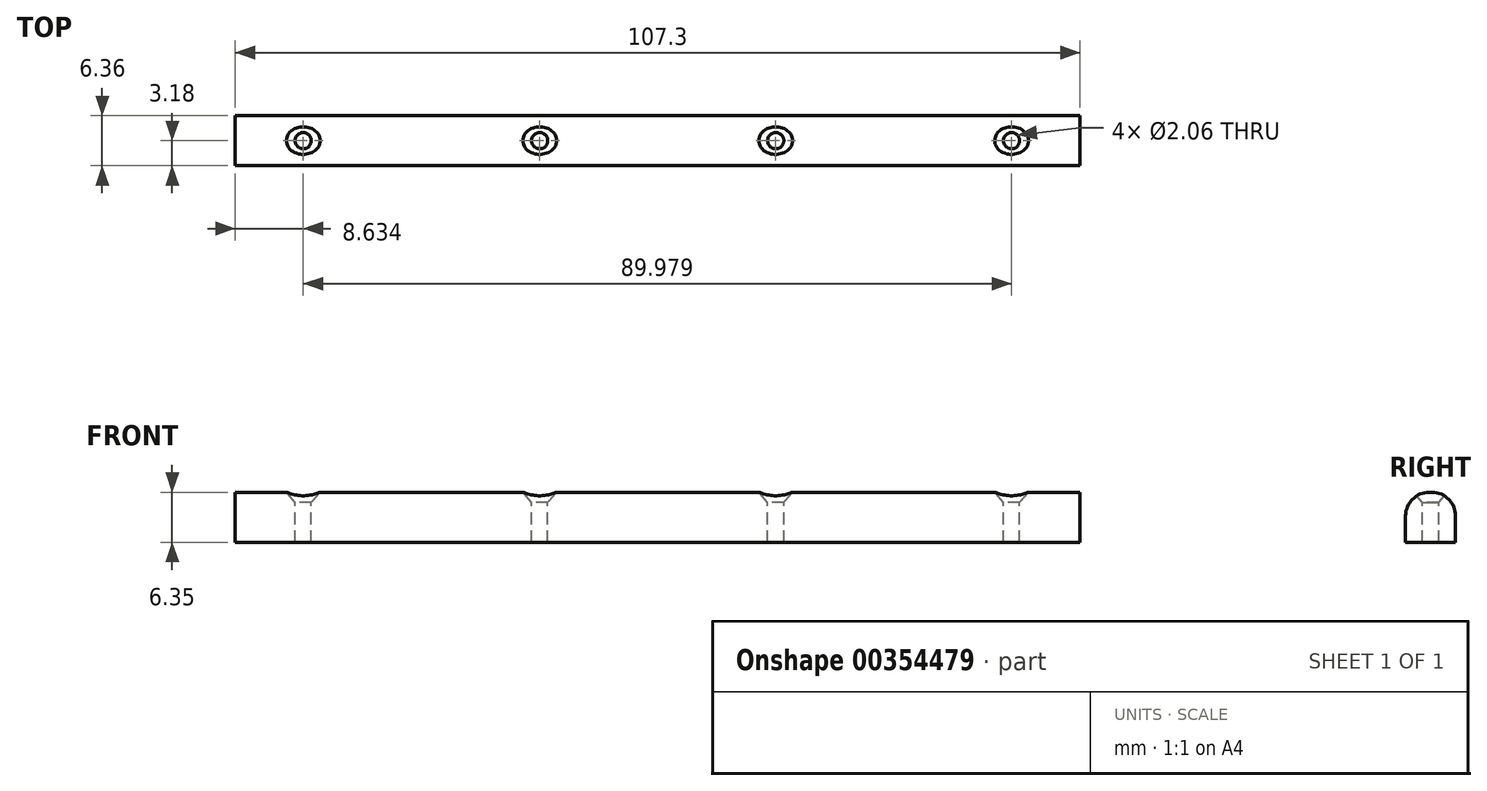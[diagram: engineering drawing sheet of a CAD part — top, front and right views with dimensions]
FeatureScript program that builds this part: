
annotation { "Feature Type Name" : "Feature", "Feature Type Description" : "" }
export const myFeature = defineFeature(function(context is Context, id is Id, definition is map)
    precondition{}
    {
        {
            var Q0;
            Q0=qCreatedBy(makeId("Top.planeOp"),FACE);
            var sketch = newSketch(context, id + "F0", { "sketchPlane" : qUnion([Q0])});
            skLineSegment(sketch, "E0.bottom", {"start": v(-53.65, 3.17) * mm, "end": v(53.65, 3.17) * mm});
            skLineSegment(sketch, "E0.top", {"start": v(-53.65, -3.17) * mm, "end": v(53.65, -3.17) * mm});
            skLineSegment(sketch, "E0.left", {"start": v(-53.65, 3.17) * mm, "end": v(-53.65, -3.17) * mm});
            skLineSegment(sketch, "E0.right", {"start": v(53.65, 3.17) * mm, "end": v(53.65, -3.18) * mm});
            skPoint(sketch, "E1", {"position": v(-45, 0) * mm});
            skPoint(sketch, "E2", {"position": v(-15, 0) * mm});
            skPoint(sketch, "E3", {"position": v(15, 0) * mm});
            skPoint(sketch, "E4", {"position": v(45, 0) * mm});
            skSolve(sketch);
        }
        {
            var Q0;
            Q0=makeQuery(id+"F0.imprint","IMPRINT",FACE,{"disambiguationData":[TD([[makeQuery(id+"F0.imprint","IMPRINT",EDGE,{"derivedFrom":sQuery(id+"F0.wireOp",EDGE,"E0.bottom")}),-1.0]])]});
            extrude(context, id + "F1", {"entities" : qUnion([Q0]), "depth" : 6.35 * mm});
        }
        {
            var Q0;
            Q0=makeQuery(id+"F1.opExtrude","CAP_EDGE",EDGE,{"disambiguationData":[OSD([sQuery(id+"F0.wireOp",EDGE,"E0.bottom")])],"isStart":false});
            var Q1;
            Q1=makeQuery(id+"F1.opExtrude","CAP_EDGE",EDGE,{"disambiguationData":[OSD([sQuery(id+"F0.wireOp",EDGE,"E0.top")])],"isStart":false});
            fillet(context, id + "F2", {"entities" : qUnion([Q0, Q1]), "radius" : 3 * mm, "tangentPropagation" : true, "allowEdgeOverflow" : false});
        }
        {
            var Q0;
            Q0=makeQuery(id+"F1.opExtrude","CAP_FACE",FACE,{"disambiguationData":[OSD([sQuery(id+"F0.wireOp",EDGE,"E0.bottom"),sQuery(id+"F0.wireOp",EDGE,"E0.top"),sQuery(id+"F0.wireOp",EDGE,"E0.left"),sQuery(id+"F0.wireOp",EDGE,"E0.right")])],"isStart":false});
            var sketch = newSketch(context, id + "F3", { "sketchPlane" : qUnion([Q0])});
            skPoint(sketch, "E5", {"position": v(-14.98, 0) * mm});
            skPoint(sketch, "E6", {"position": v(0, 0) * mm});
            skPoint(sketch, "E7", {"position": v(-45.02, 0) * mm});
            skPoint(sketch, "E8", {"position": v(15, 0) * mm});
            skPoint(sketch, "E9", {"position": v(44.96, 0) * mm});
            skSolve(sketch);
        }
        {
            var Q0;
            Q0=sQuery(id+"F3.wireOp",VERTEX,"E5");
            var Q1;
            Q1=sQuery(id+"F3.wireOp",VERTEX,"E8");
            var Q2;
            Q2=sQuery(id+"F3.wireOp",VERTEX,"E9");
            var Q3;
            Q3=sQuery(id+"F3.wireOp",VERTEX,"E7");
            var Q4;
            Q4=makeQuery(id+"F1.opExtrude","SWEPT_BODY",BODY,{"disambiguationData":[OSD([sQuery(id+"F0.wireOp",EDGE,"E0.bottom"),sQuery(id+"F0.wireOp",EDGE,"E0.top"),sQuery(id+"F0.wireOp",EDGE,"E0.left"),sQuery(id+"F0.wireOp",EDGE,"E0.right")])]});
            hole(context, id + "F4", {"style" : HoleStyle.C_SINK, "endStyle" : HoleEndStyle.THROUGH, "standardTappedOrClearance" : lookupTablePath({ "standard" : "ANSI", "fit" : "Normal (ASME)", "size" : "#1", "type" : "Clearance" }), "standardBlindInLast" : lookupTablePath({ "fit" : "Free", "standard" : "ANSI", "size" : "#1", "type" : "Clearance" }), "holeDiameter" : 2.06 * mm, "cSinkDiameter" : 4.27 * mm, "cSinkAngle" : 82 * degree, "isTappedThrough" : true, "tappedDepth" : 12 * mm, "tapClearance" : 3, "startFromSketch" : true, "locations" : qUnion([Q0, Q1, Q2, Q3]), "scope" : qUnion([Q4])});
        }
    });
